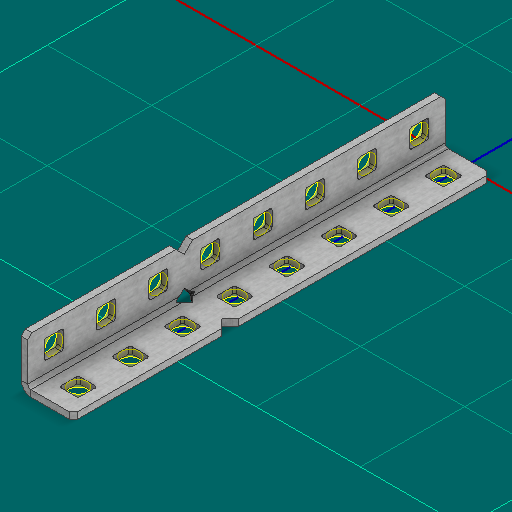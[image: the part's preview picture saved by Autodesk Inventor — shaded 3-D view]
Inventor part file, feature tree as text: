
AUTODESK INVENTOR PART (.ipt)
format: ipt  version: 2025 (Build 290162000, 162)  size: 501,248 bytes
history: native  units: in
note: dims shown in document units (in); Inventor stores cm internally (conversion verified against a paired STEP export)
features: other x41, sketch x2, sheet_metal_op x1
ambient origin geometry x8: Origin, YZ Plane, XZ Plane, XY Plane, X Axis, Y Axis, Z Axis, Center Point
bodies: Solid1 (feature_tree)
feature tree (44):
  other  "Alu Angle 1x1x8.ipt"
  other  "Solid1::Alu Angle 1x1x8.ipt"
  other  "TaggingFeature1"
  sketch  "Sketch1"  dims[d0=0.3937in]
  sketch  "Sketch2"  dims[d1=0.0625in]
  sheet_metal_op  "Body Pattern Sketch"
  other  "Arc Length"
  other  "Diagonal Plane"
  other  "Srf1"
  other  "Srf2"
  other  "Srf3"
  other  "Srf4"
  other  "Srf5"
  other  "Srf6"
  other  "Srf7"
  other  "Srf8"
  other  "Srf9"
  other  "Srf10"
  other  "Srf11"
  other  "Srf12"
  other  "Srf13"
  other  "Srf14"
  other  "Srf15"
  other  "Srf16"
  other  "Srf17"
  other  "Srf18"
  other  "Srf91::Derived"
  other  "Srf92::Derived"
  other  "Srf856::Derived"
  other  "Srf857::Derived"
  other  "Srf858::Derived"
  other  "Srf859::Derived"
  other  "Srf860::Derived"
  other  "Srf861::Derived"
  other  "Srf1383::Derived"
  other  "Srf1275::Derived"
  other  "Srf1276::Derived"
  other  "Srf1278::Derived"
  other  "Srf1279::Derived"
  other  "Srf1280::Derived"
  other  "Srf1281::Derived"
  other  "Srf1282::Derived"
  other  "Srf1283::Derived"
  other  "Srf1475::Derived"
